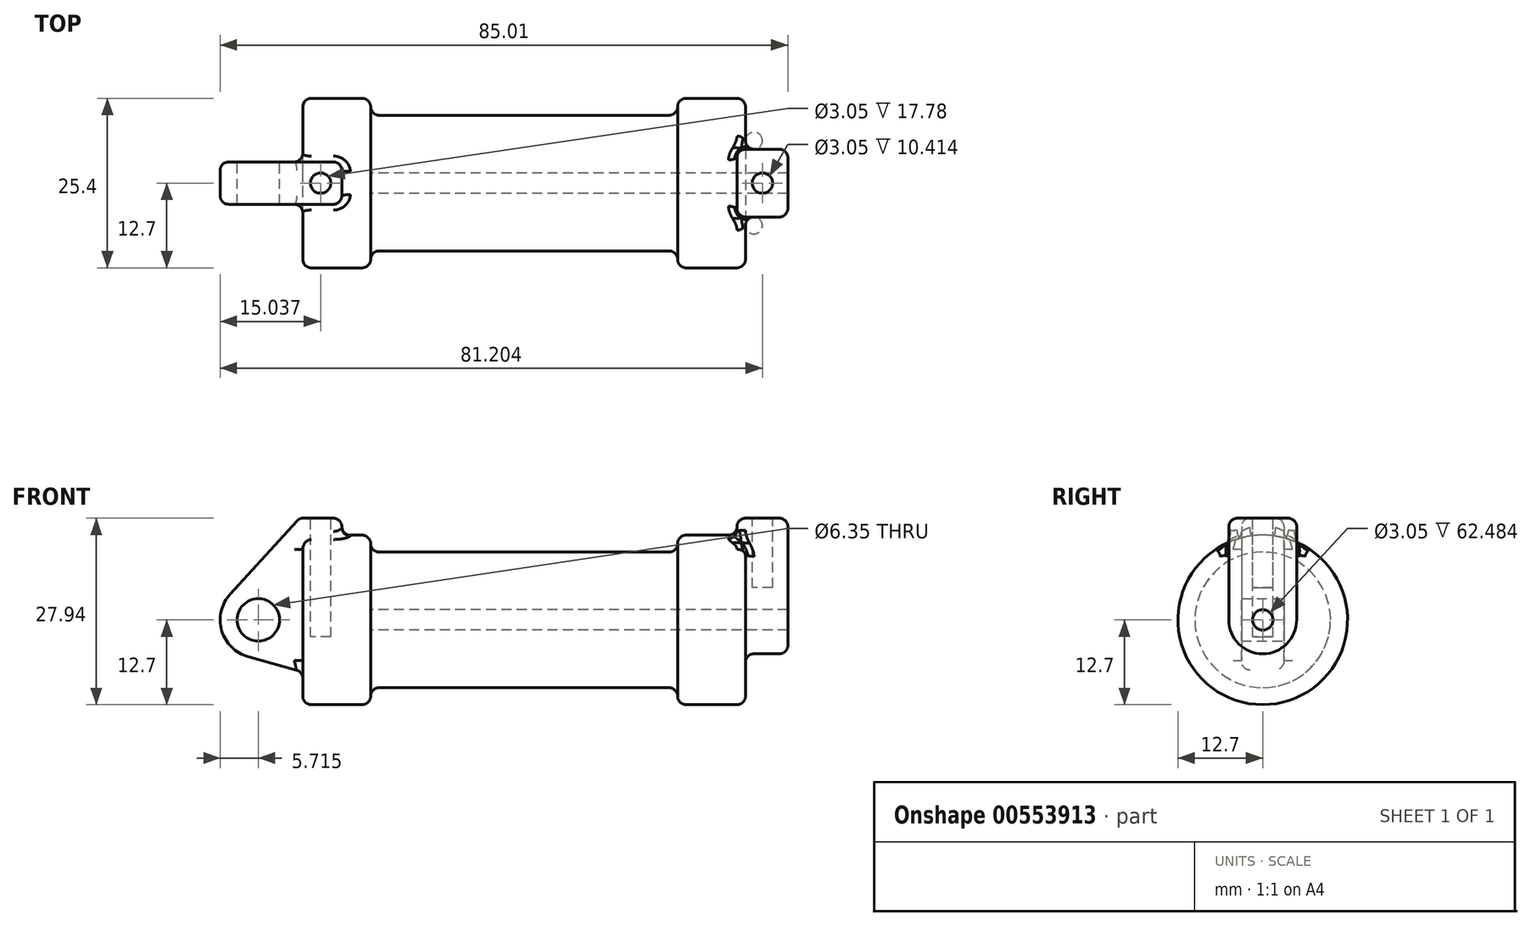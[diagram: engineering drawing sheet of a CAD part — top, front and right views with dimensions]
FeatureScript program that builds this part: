
annotation { "Feature Type Name" : "Feature", "Feature Type Description" : "" }
export const myFeature = defineFeature(function(context is Context, id is Id, definition is map)
    precondition{}
    {
        {
            var Q0;
            Q0=qCreatedBy(makeId("Front.planeOp"),FACE);
            var sketch = newSketch(context, id + "F0", { "sketchPlane" : qUnion([Q0])});
            skLineSegment(sketch, "E0", {"start": v(0, 0) * mm, "end": v(0, 12.7) * mm});
            skLineSegment(sketch, "E1", {"start": v(0, 12.7) * mm, "end": v(10.16, 12.7) * mm});
            skLineSegment(sketch, "E2", {"start": v(10.16, 12.7) * mm, "end": v(10.16, 10.16) * mm});
            skLineSegment(sketch, "E3", {"start": v(10.16, 10.16) * mm, "end": v(56.13, 10.16) * mm});
            skLineSegment(sketch, "E4", {"start": v(56.13, 10.16) * mm, "end": v(56.13, 12.7) * mm});
            skLineSegment(sketch, "E5", {"start": v(56.13, 12.7) * mm, "end": v(66.3, 12.7) * mm});
            skLineSegment(sketch, "E6", {"start": v(66.3, 12.7) * mm, "end": v(66.3, 0) * mm});
            skLineSegment(sketch, "E7", {"start": v(66.3, 0) * mm, "end": v(0, 0) * mm});
            skLineSegment(sketch, "E8", {"start": v(5.84, 15.24) * mm, "end": v(-0.5, 15.24) * mm});
            skLineSegment(sketch, "E9", {"start": v(-0.5, 15.24) * mm, "end": v(-10.88, 3.85) * mm});
            skLineSegment(sketch, "E10", {"start": v(0, 0) * mm, "end": v(-6.65, 0) * mm});
            skCircle(sketch, "E11", {"center": v(-6.65, 0) * mm, "radius": 5.72 * mm});
            skCircle(sketch, "E12", {"center": v(-6.65, 0) * mm, "radius": 3.18 * mm});
            skLineSegment(sketch, "E13", {"start": v(5.84, 15.24) * mm, "end": v(5.84, -9.4) * mm});
            skLineSegment(sketch, "E14", {"start": v(5.84, -9.4) * mm, "end": v(-8.18, -5.5) * mm});
            skSolve(sketch);
        }
        {
            var Q0;
            {var subQ0=sQuery(id+"F0.wireOp",EDGE,"E2");Q0=makeQuery(id+"F0.imprint","IMPRINT",FACE,{"disambiguationData":[TD([[makeQuery(id+"F0.imprint","IMPRINT",EDGE,{"derivedFrom":subQ0}),-1.0]])]});}
            var Q1;
            {var subQ0=sQuery(id+"F0.wireOp",EDGE,"E0");Q1=makeQuery(id+"F0.imprint","IMPRINT",FACE,{"disambiguationData":[TD([[makeQuery(id+"F0.imprint","IMPRINT",EDGE,{"derivedFrom":subQ0}),-1.0]])]});}
            var Q2;
            Q2=sQuery(id+"F0.wireOp",EDGE,"E7");
            revolve(context, id + "F1", {"entities" : qUnion([Q0, Q1]), "axis" : qUnion([Q2]), "revolveType" : RevolveType.FULL});
        }
        {
            var Q0;
            {var subQ5=sQuery(id+"F0.wireOp",EDGE,"E12");Q0=makeQuery(id+"F0.imprint","IMPRINT",FACE,{"disambiguationData":[TD([[makeQuery(id+"F0.imprint","IMPRINT",EDGE,{"derivedFrom":subQ5}),-1.0]])]});}
            var Q1;
            {var subQ0=sQuery(id+"F0.wireOp",EDGE,"E14");Q1=makeQuery(id+"F0.imprint","IMPRINT",FACE,{"disambiguationData":[TD([[makeQuery(id+"F0.imprint","IMPRINT",EDGE,{"derivedFrom":subQ0}),-1.0]])]});}
            var Q2;
            {var subQ1=sQuery(id+"F0.wireOp",EDGE,"E0");Q2=makeQuery(id+"F0.imprint","IMPRINT",FACE,{"disambiguationData":[TD([[makeQuery(id+"F0.imprint","IMPRINT",EDGE,{"derivedFrom":subQ1}),1.0]])]});}
            var Q3;
            {var subQ0=sQuery(id+"F0.wireOp",EDGE,"E0");Q3=makeQuery(id+"F0.imprint","IMPRINT",FACE,{"disambiguationData":[TD([[makeQuery(id+"F0.imprint","IMPRINT",EDGE,{"derivedFrom":subQ0}),-1.0]])]});}
            extrude(context, id + "F2", {"entities" : qUnion([Q0, Q1, Q2, Q3]), "operationType" : NewBodyOperationType.ADD, "endBound" : BoundingType.SYMMETRIC, "depth" : 6.35 * mm, "offsetDistance" : 25.4 * mm});
        }
        {
            var Q0;
            Q0=makeQuery(id+"F1.opRevolve","SWEPT_FACE",FACE,{"disambiguationData":[OSD([sQuery(id+"F0.wireOp",EDGE,"E6")])]});
            var sketch = newSketch(context, id + "F3", { "sketchPlane" : qUnion([Q0])});
            skCircle(sketch, "E15", {"center": v(0, 0) * mm, "radius": 1.52 * mm});
            skCircle(sketch, "E16", {"center": v(0, 0) * mm, "radius": 5.08 * mm});
            skLineSegment(sketch, "E17", {"start": v(-5.08, 0) * mm, "end": v(-5.08, 15.24) * mm});
            skLineSegment(sketch, "E18", {"start": v(-5.08, 15.24) * mm, "end": v(5.08, 15.24) * mm});
            skLineSegment(sketch, "E19", {"start": v(5.08, 0) * mm, "end": v(5.08, 15.24) * mm});
            skSolve(sketch);
        }
        {
            var Q0;
            {var subQ0=sQuery(id+"F3.wireOp",EDGE,"E17");var subQ1=sQuery(id+"F3.wireOp",EDGE,"E16");var subQ2=makeQuery(id+"F3.imprint","INTERSECT",VERTEX,{"derivedFrom":[subQ1,subQ0]});Q0=makeQuery(id+"F3.imprint","IMPRINT",FACE,{"disambiguationData":[TD([[makeQuery(id+"F3.imprint","IMPRINT",EDGE,{"disambiguationData":[TD([[subQ2,1.0]])],"derivedFrom":subQ1}),-1.0]])]});}
            var Q1;
            {var subQ0=sQuery(id+"F3.wireOp",EDGE,"E18");Q1=makeQuery(id+"F3.imprint","IMPRINT",FACE,{"disambiguationData":[TD([[makeQuery(id+"F3.imprint","IMPRINT",EDGE,{"derivedFrom":subQ0}),-1.0]])]});}
            var Q2;
            Q2=makeQuery(id+"F3.imprint","IMPRINT",FACE,{"disambiguationData":[TD([[makeQuery(id+"F3.imprint","IMPRINT",EDGE,{"derivedFrom":sQuery(id+"F3.wireOp",EDGE,"E15")}),-1.0]])]});
            extrude(context, id + "F4", {"entities" : qUnion([Q0, Q1, Q2]), "operationType" : NewBodyOperationType.ADD, "depth" : 6.35 * mm, "offsetDistance" : 25.4 * mm, "hasSecondDirection" : true, "secondDirectionOppositeDirection" : true, "secondDirectionDepth" : 1.27 * mm});
        }
        {
            var Q0;
            Q0=makeQuery(id+"F4.boolean.opBoolean","SPLIT",FACE,{"disambiguationData":[TD([makeQuery(id+"F4.opExtrude","SWEPT_FACE",FACE,{"disambiguationData":[OSD([sQuery(id+"F3.wireOp",EDGE,"E15")])]})])],"derivedFrom":makeQuery(id+"F1.opRevolve","SWEPT_FACE",FACE,{"disambiguationData":[OSD([sQuery(id+"F0.wireOp",EDGE,"E6")])]})});
            var Q1;
            Q1=makeQuery(id+"F1.opRevolve","SWEPT_FACE",FACE,{"disambiguationData":[OSD([sQuery(id+"F0.wireOp",EDGE,"E2")])]});
            extrude(context, id + "F5", {"entities" : qUnion([Q0]), "operationType" : NewBodyOperationType.REMOVE, "endBound" : BoundingType.UP_TO_SURFACE, "oppositeDirection" : true, "depth" : 25.4 * mm, "endBoundEntityFace" : qUnion([Q1]), "offsetDistance" : 25.4 * mm});
        }
        {
            var Q0;
            Q0=makeQuery(id+"F2.opExtrude","SWEPT_FACE",FACE,{"disambiguationData":[OSD([sQuery(id+"F0.wireOp",EDGE,"E8")])]});
            var sketch = newSketch(context, id + "F6", { "sketchPlane" : qUnion([Q0])});
            skCircle(sketch, "E20", {"center": v(2.67, 0) * mm, "radius": 1.52 * mm});
            skPoint(sketch, "E20.centerSnap0", {"position": v(5.84, 0) * mm});
            skPoint(sketch, "E20.centerSnap1", {"position": v(2.67, 3.18) * mm});
            skSolve(sketch);
        }
        {
            var Q0;
            Q0=makeQuery(id+"F4.opExtrude","SWEPT_FACE",FACE,{"disambiguationData":[OSD([sQuery(id+"F3.wireOp",EDGE,"E18")])]});
            var sketch = newSketch(context, id + "F7", { "sketchPlane" : qUnion([Q0])});
            skCircle(sketch, "E21", {"center": v(68.83, 0) * mm, "radius": 1.52 * mm});
            skPoint(sketch, "E21.centerSnap0", {"position": v(72.64, 0) * mm});
            skPoint(sketch, "E21.centerSnap1", {"position": v(68.83, 5.08) * mm});
            skSolve(sketch);
        }
        {
            var Q0;
            Q0=makeQuery(id+"F6.imprint","IMPRINT",FACE,{"disambiguationData":[TD([[makeQuery(id+"F6.imprint","IMPRINT",EDGE,{"derivedFrom":sQuery(id+"F6.wireOp",EDGE,"E20")}),1.0]])]});
            extrude(context, id + "F8", {"entities" : qUnion([Q0]), "operationType" : NewBodyOperationType.REMOVE, "oppositeDirection" : true, "depth" : 17.78 * mm, "offsetDistance" : 25.4 * mm});
        }
        {
            var Q0;
            Q0=makeQuery(id+"F7.imprint","IMPRINT",FACE,{"disambiguationData":[TD([[makeQuery(id+"F7.imprint","IMPRINT",EDGE,{"derivedFrom":sQuery(id+"F7.wireOp",EDGE,"E21")}),1.0]])]});
            extrude(context, id + "F9", {"entities" : qUnion([Q0]), "operationType" : NewBodyOperationType.REMOVE, "oppositeDirection" : true, "depth" : 10.4 * mm, "offsetDistance" : 25.4 * mm});
        }
        {
            var Q0;
            Q0=makeQuery(id+"F2.opExtrude","CAP_EDGE",EDGE,{"disambiguationData":[OSD([sQuery(id+"F0.wireOp",EDGE,"E8")])],"isStart":false});
            var Q1;
            Q1=makeQuery(id+"F2.opExtrude","SWEPT_EDGE",EDGE,{"disambiguationData":[OSD([sQuery(id+"F0.wireOp",EDGE,"E8"),sQuery(id+"F0.wireOp",EDGE,"E13")])]});
            var Q2;
            Q2=makeQuery(id+"F2.opExtrude","CAP_EDGE",EDGE,{"disambiguationData":[OSD([sQuery(id+"F0.wireOp",EDGE,"E8")])],"isStart":true});
            var Q3;
            Q3=makeQuery(id+"F2.opExtrude","SWEPT_EDGE",EDGE,{"disambiguationData":[OSD([sQuery(id+"F0.wireOp",EDGE,"E8"),sQuery(id+"F0.wireOp",EDGE,"E9")])]});
            var Q4;
            Q4=makeQuery(id+"F2.opExtrude","CAP_EDGE",EDGE,{"disambiguationData":[OSD([sQuery(id+"F0.wireOp",EDGE,"E9")])],"isStart":true});
            var Q5;
            Q5=makeQuery(id+"F2.opExtrude","CAP_EDGE",EDGE,{"disambiguationData":[OSD([sQuery(id+"F0.wireOp",EDGE,"E9")])],"isStart":false});
            var Q6;
            Q6=makeQuery(id+"F2.opExtrude","SWEPT_EDGE",EDGE,{"disambiguationData":[OSD([sQuery(id+"F0.wireOp",EDGE,"E9"),sQuery(id+"F0.wireOp",EDGE,"E11")])]});
            var Q7;
            Q7=makeQuery(id+"F2.opExtrude","CAP_EDGE",EDGE,{"disambiguationData":[OSD([sQuery(id+"F0.wireOp",EDGE,"E11")])],"isStart":false});
            var Q8;
            Q8=makeQuery(id+"F2.boolean.opBoolean","INTERSECT",EDGE,{"derivedFrom":[makeQuery(id+"F1.opRevolve","SWEPT_FACE",FACE,{"disambiguationData":[OSD([sQuery(id+"F0.wireOp",EDGE,"E0")])]}),makeQuery(id+"F2.opExtrude","CAP_FACE",FACE,{"disambiguationData":[OSD([sQuery(id+"F0.wireOp",EDGE,"E8"),sQuery(id+"F0.wireOp",EDGE,"E9"),sQuery(id+"F0.wireOp",EDGE,"E11"),sQuery(id+"F0.wireOp",EDGE,"E12"),sQuery(id+"F0.wireOp",EDGE,"E13"),sQuery(id+"F0.wireOp",EDGE,"E14")])],"isStart":true})]});
            var Q9;
            Q9=makeQuery(id+"F2.boolean.opBoolean","INTERSECT",EDGE,{"derivedFrom":[makeQuery(id+"F1.opRevolve","SWEPT_FACE",FACE,{"disambiguationData":[OSD([sQuery(id+"F0.wireOp",EDGE,"E0")])]}),makeQuery(id+"F2.opExtrude","SWEPT_FACE",FACE,{"disambiguationData":[OSD([sQuery(id+"F0.wireOp",EDGE,"E14")])]})]});
            var Q10;
            Q10=makeQuery(id+"F2.opExtrude","CAP_EDGE",EDGE,{"disambiguationData":[OSD([sQuery(id+"F0.wireOp",EDGE,"E11")])],"isStart":true});
            var Q11;
            Q11=makeQuery(id+"F2.opExtrude","SWEPT_EDGE",EDGE,{"disambiguationData":[OSD([sQuery(id+"F0.wireOp",EDGE,"E11"),sQuery(id+"F0.wireOp",EDGE,"E14")])]});
            var Q12;
            Q12=makeQuery(id+"F2.opExtrude","CAP_EDGE",EDGE,{"disambiguationData":[OSD([sQuery(id+"F0.wireOp",EDGE,"E14")])],"isStart":true});
            var Q13;
            Q13=makeQuery(id+"F2.opExtrude","CAP_EDGE",EDGE,{"disambiguationData":[OSD([sQuery(id+"F0.wireOp",EDGE,"E14")])],"isStart":false});
            var Q14;
            Q14=makeQuery(id+"F1.opRevolve","SWEPT_EDGE",EDGE,{"disambiguationData":[OSD([sQuery(id+"F0.wireOp",EDGE,"E0"),sQuery(id+"F0.wireOp",EDGE,"E1")])]});
            var Q15;
            Q15=makeQuery(id+"F2.boolean.opBoolean","INTERSECT",EDGE,{"derivedFrom":[makeQuery(id+"F1.opRevolve","SWEPT_FACE",FACE,{"disambiguationData":[OSD([sQuery(id+"F0.wireOp",EDGE,"E0")])]}),makeQuery(id+"F2.opExtrude","CAP_FACE",FACE,{"disambiguationData":[OSD([sQuery(id+"F0.wireOp",EDGE,"E8"),sQuery(id+"F0.wireOp",EDGE,"E9"),sQuery(id+"F0.wireOp",EDGE,"E11"),sQuery(id+"F0.wireOp",EDGE,"E12"),sQuery(id+"F0.wireOp",EDGE,"E13"),sQuery(id+"F0.wireOp",EDGE,"E14")])],"isStart":false})]});
            var Q16;
            Q16=makeQuery(id+"F2.opExtrude","CAP_EDGE",EDGE,{"disambiguationData":[OSD([sQuery(id+"F0.wireOp",EDGE,"E13")])],"isStart":false});
            var Q17;
            Q17=makeQuery(id+"F2.boolean.opBoolean","INTERSECT",EDGE,{"derivedFrom":[makeQuery(id+"F1.opRevolve","SWEPT_FACE",FACE,{"disambiguationData":[OSD([sQuery(id+"F0.wireOp",EDGE,"E1")])]}),makeQuery(id+"F2.opExtrude","CAP_FACE",FACE,{"disambiguationData":[OSD([sQuery(id+"F0.wireOp",EDGE,"E8"),sQuery(id+"F0.wireOp",EDGE,"E9"),sQuery(id+"F0.wireOp",EDGE,"E11"),sQuery(id+"F0.wireOp",EDGE,"E12"),sQuery(id+"F0.wireOp",EDGE,"E13"),sQuery(id+"F0.wireOp",EDGE,"E14")])],"isStart":false})]});
            var Q18;
            Q18=makeQuery(id+"F1.opRevolve","SWEPT_EDGE",EDGE,{"disambiguationData":[OSD([sQuery(id+"F0.wireOp",EDGE,"E1"),sQuery(id+"F0.wireOp",EDGE,"E2")])]});
            var Q19;
            Q19=makeQuery(id+"F2.boolean.opBoolean","INTERSECT",EDGE,{"derivedFrom":[makeQuery(id+"F1.opRevolve","SWEPT_FACE",FACE,{"disambiguationData":[OSD([sQuery(id+"F0.wireOp",EDGE,"E1")])]}),makeQuery(id+"F2.opExtrude","CAP_FACE",FACE,{"disambiguationData":[OSD([sQuery(id+"F0.wireOp",EDGE,"E8"),sQuery(id+"F0.wireOp",EDGE,"E9"),sQuery(id+"F0.wireOp",EDGE,"E11"),sQuery(id+"F0.wireOp",EDGE,"E12"),sQuery(id+"F0.wireOp",EDGE,"E13"),sQuery(id+"F0.wireOp",EDGE,"E14")])],"isStart":true})]});
            var Q20;
            Q20=makeQuery(id+"F2.opExtrude","CAP_EDGE",EDGE,{"disambiguationData":[OSD([sQuery(id+"F0.wireOp",EDGE,"E13")])],"isStart":true});
            var Q21;
            Q21=makeQuery(id+"F2.boolean.opBoolean","INTERSECT",EDGE,{"derivedFrom":[makeQuery(id+"F1.opRevolve","SWEPT_FACE",FACE,{"disambiguationData":[OSD([sQuery(id+"F0.wireOp",EDGE,"E1")])]}),makeQuery(id+"F2.opExtrude","SWEPT_FACE",FACE,{"disambiguationData":[OSD([sQuery(id+"F0.wireOp",EDGE,"E13")])]})]});
            var Q22;
            Q22=makeQuery(id+"F4.opExtrude","CAP_EDGE",EDGE,{"disambiguationData":[OSD([sQuery(id+"F3.wireOp",EDGE,"E19")])],"isStart":false});
            var Q23;
            Q23=makeQuery(id+"F4.opExtrude","CAP_EDGE",EDGE,{"disambiguationData":[OSD([sQuery(id+"F3.wireOp",EDGE,"E17")])],"isStart":false});
            var Q24;
            Q24=makeQuery(id+"F4.opExtrude","CAP_EDGE",EDGE,{"disambiguationData":[OSD([sQuery(id+"F3.wireOp",EDGE,"E16")])],"isStart":false});
            var Q25;
            Q25=makeQuery(id+"F4.boolean.opBoolean","INTERSECT",EDGE,{"derivedFrom":[makeQuery(id+"F1.opRevolve","SWEPT_FACE",FACE,{"disambiguationData":[OSD([sQuery(id+"F0.wireOp",EDGE,"E6")])]}),makeQuery(id+"F4.opExtrude","SWEPT_FACE",FACE,{"disambiguationData":[OSD([sQuery(id+"F3.wireOp",EDGE,"E19")])]})]});
            var Q26;
            Q26=makeQuery(id+"F4.opExtrude","SWEPT_EDGE",EDGE,{"disambiguationData":[OSD([sQuery(id+"F3.wireOp",EDGE,"E18"),sQuery(id+"F3.wireOp",EDGE,"E19")])]});
            var Q27;
            Q27=makeQuery(id+"F4.opExtrude","CAP_EDGE",EDGE,{"disambiguationData":[OSD([sQuery(id+"F3.wireOp",EDGE,"E18")])],"isStart":false});
            var Q28;
            Q28=makeQuery(id+"F4.opExtrude","CAP_EDGE",EDGE,{"disambiguationData":[OSD([sQuery(id+"F3.wireOp",EDGE,"E18")])],"isStart":true});
            var Q29;
            Q29=makeQuery(id+"F4.opExtrude","SWEPT_EDGE",EDGE,{"disambiguationData":[OSD([sQuery(id+"F3.wireOp",EDGE,"E17"),sQuery(id+"F3.wireOp",EDGE,"E18")])]});
            var Q30;
            Q30=makeQuery(id+"F4.boolean.opBoolean","INTERSECT",EDGE,{"derivedFrom":[makeQuery(id+"F1.opRevolve","SWEPT_FACE",FACE,{"disambiguationData":[OSD([sQuery(id+"F0.wireOp",EDGE,"E5")])]}),makeQuery(id+"F4.opExtrude","SWEPT_FACE",FACE,{"disambiguationData":[OSD([sQuery(id+"F3.wireOp",EDGE,"E19")])]})]});
            var Q31;
            Q31=makeQuery(id+"F4.opExtrude","CAP_EDGE",EDGE,{"disambiguationData":[OSD([sQuery(id+"F3.wireOp",EDGE,"E19")])],"isStart":true});
            var Q32;
            Q32=makeQuery(id+"F1.opRevolve","SWEPT_EDGE",EDGE,{"disambiguationData":[OSD([sQuery(id+"F0.wireOp",EDGE,"E4"),sQuery(id+"F0.wireOp",EDGE,"E5")])]});
            var Q33;
            Q33=makeQuery(id+"F1.opRevolve","SWEPT_EDGE",EDGE,{"disambiguationData":[OSD([sQuery(id+"F0.wireOp",EDGE,"E3"),sQuery(id+"F0.wireOp",EDGE,"E4")])]});
            var Q34;
            Q34=makeQuery(id+"F1.opRevolve","SWEPT_EDGE",EDGE,{"disambiguationData":[OSD([sQuery(id+"F0.wireOp",EDGE,"E2"),sQuery(id+"F0.wireOp",EDGE,"E3")])]});
            var Q35;
            Q35=makeQuery(id+"F1.opRevolve","SWEPT_EDGE",EDGE,{"disambiguationData":[OSD([sQuery(id+"F0.wireOp",EDGE,"E5"),sQuery(id+"F0.wireOp",EDGE,"E6")])]});
            var Q36;
            Q36=makeQuery(id+"F4.boolean.opBoolean","INTERSECT",EDGE,{"derivedFrom":[makeQuery(id+"F1.opRevolve","SWEPT_FACE",FACE,{"disambiguationData":[OSD([sQuery(id+"F0.wireOp",EDGE,"E6")])]}),makeQuery(id+"F4.opExtrude","SWEPT_FACE",FACE,{"disambiguationData":[OSD([sQuery(id+"F3.wireOp",EDGE,"E17")])]})]});
            var Q37;
            Q37=makeQuery(id+"F4.boolean.opBoolean","INTERSECT",EDGE,{"derivedFrom":[makeQuery(id+"F1.opRevolve","SWEPT_FACE",FACE,{"disambiguationData":[OSD([sQuery(id+"F0.wireOp",EDGE,"E6")])]}),makeQuery(id+"F4.opExtrude","SWEPT_FACE",FACE,{"disambiguationData":[OSD([sQuery(id+"F3.wireOp",EDGE,"E16")])]})]});
            var Q38;
            Q38=makeQuery(id+"F4.opExtrude","CAP_EDGE",EDGE,{"disambiguationData":[OSD([sQuery(id+"F3.wireOp",EDGE,"E17")])],"isStart":true});
            var Q39;
            Q39=makeQuery(id+"F4.boolean.opBoolean","INTERSECT",EDGE,{"derivedFrom":[makeQuery(id+"F1.opRevolve","SWEPT_FACE",FACE,{"disambiguationData":[OSD([sQuery(id+"F0.wireOp",EDGE,"E5")])]}),makeQuery(id+"F4.opExtrude","SWEPT_FACE",FACE,{"disambiguationData":[OSD([sQuery(id+"F3.wireOp",EDGE,"E17")])]})]});
            var Q40;
            Q40=makeQuery(id+"F4.boolean.opBoolean","INTERSECT",EDGE,{"derivedFrom":[makeQuery(id+"F1.opRevolve","SWEPT_FACE",FACE,{"disambiguationData":[OSD([sQuery(id+"F0.wireOp",EDGE,"E5")])]}),makeQuery(id+"F4.opExtrude","CAP_FACE",FACE,{"disambiguationData":[OSD([sQuery(id+"F3.wireOp",EDGE,"E15"),sQuery(id+"F3.wireOp",EDGE,"E16"),sQuery(id+"F3.wireOp",EDGE,"E17"),sQuery(id+"F3.wireOp",EDGE,"E18"),sQuery(id+"F3.wireOp",EDGE,"E19")])],"isStart":true})]});
            fillet(context, id + "F10", {"entities" : qUnion([Q0, Q1, Q2, Q3, Q4, Q5, Q6, Q7, Q8, Q9, Q10, Q11, Q12, Q13, Q14, Q15, Q16, Q17, Q18, Q19, Q20, Q21, Q22, Q23, Q24, Q25, Q26, Q27, Q28, Q29, Q30, Q31, Q32, Q33, Q34, Q35, Q36, Q37, Q38, Q39, Q40]), "radius" : 1.27 * mm, "tangentPropagation" : true, "allowEdgeOverflow" : false});
        }
    });
